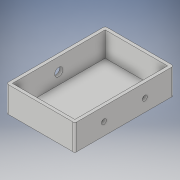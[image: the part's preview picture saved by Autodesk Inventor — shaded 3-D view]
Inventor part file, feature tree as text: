
AUTODESK INVENTOR PART (.ipt)
format: ipt  version: 2017 SP1 (Build 210196100, 196)  size: 167,424 bytes
history: native  units: in
note: dims shown in document units (in); Inventor stores cm internally (conversion verified against a paired STEP export)
features: sketch x5, extrude x2, hole x2, projected_geometry x2, chamfer x1, fillet x1
ambient origin geometry x8: Origin, YZ Plane, XZ Plane, XY Plane, X Axis, Y Axis, Z Axis, Center Point
bodies: Solid1 (feature_tree)
feature tree (13):
  extrude  "Extrusion1"  Depth=2.0in
  extrude  "Extrusion2"  Depth=0.6in
  sketch  "Sketch5"  dims[d4=0.6in d5=0.6in]
  hole  "Hole1"  [1 undecoded]
  hole  "Hole2"  [1 undecoded]
  chamfer  "Chamfer1"  Distance=1.5in
  fillet  "Fillet1"  Radius=2.704in
  sketch  "Sketch3"  dims[d0=3.0in d1=2.0in]
  sketch  "Sketch4"  dims[d2=0.6in d3=0.6in]
  projected_geometry  "Projected Loop1"
  projected_geometry  "Projected Loop2"
  sketch  "Sketch6"  dims[d6=0.85in d7=0.125in d8=0.0in]
  sketch  "Sketch7"  dims[d9=0.19in d10=1.5in d11=0.0in d12=2.704in d13=1.904in d14=1.904in d15=0.558in d16=0.431in d17=0.431in d18=0.558in d19=1.0in d20=0.8125in d21=0.8125in d22=1.775in d23=1.775in d24=2.5in d25=0.3in d26=0.75in d27=0.375in d28=0.25in d29=0.5635in d30=1.0in d31=0.8108in d32=0.8125in d33=0.8125in d34=3.025in d35=3.025in d36=0.5in d37=0.75in d38=0.375in d39=0.25in d40=0.5635in d41=1.0in d42=0.8108in d43=0.05in d44=0.125in d45=45.0deg d46=0.125in]
note: 2 required parameter values undecoded (feature->parameter linkage not recoverable at this tier; creation-order binding heuristic only, values carry confidence <= 0.55)
